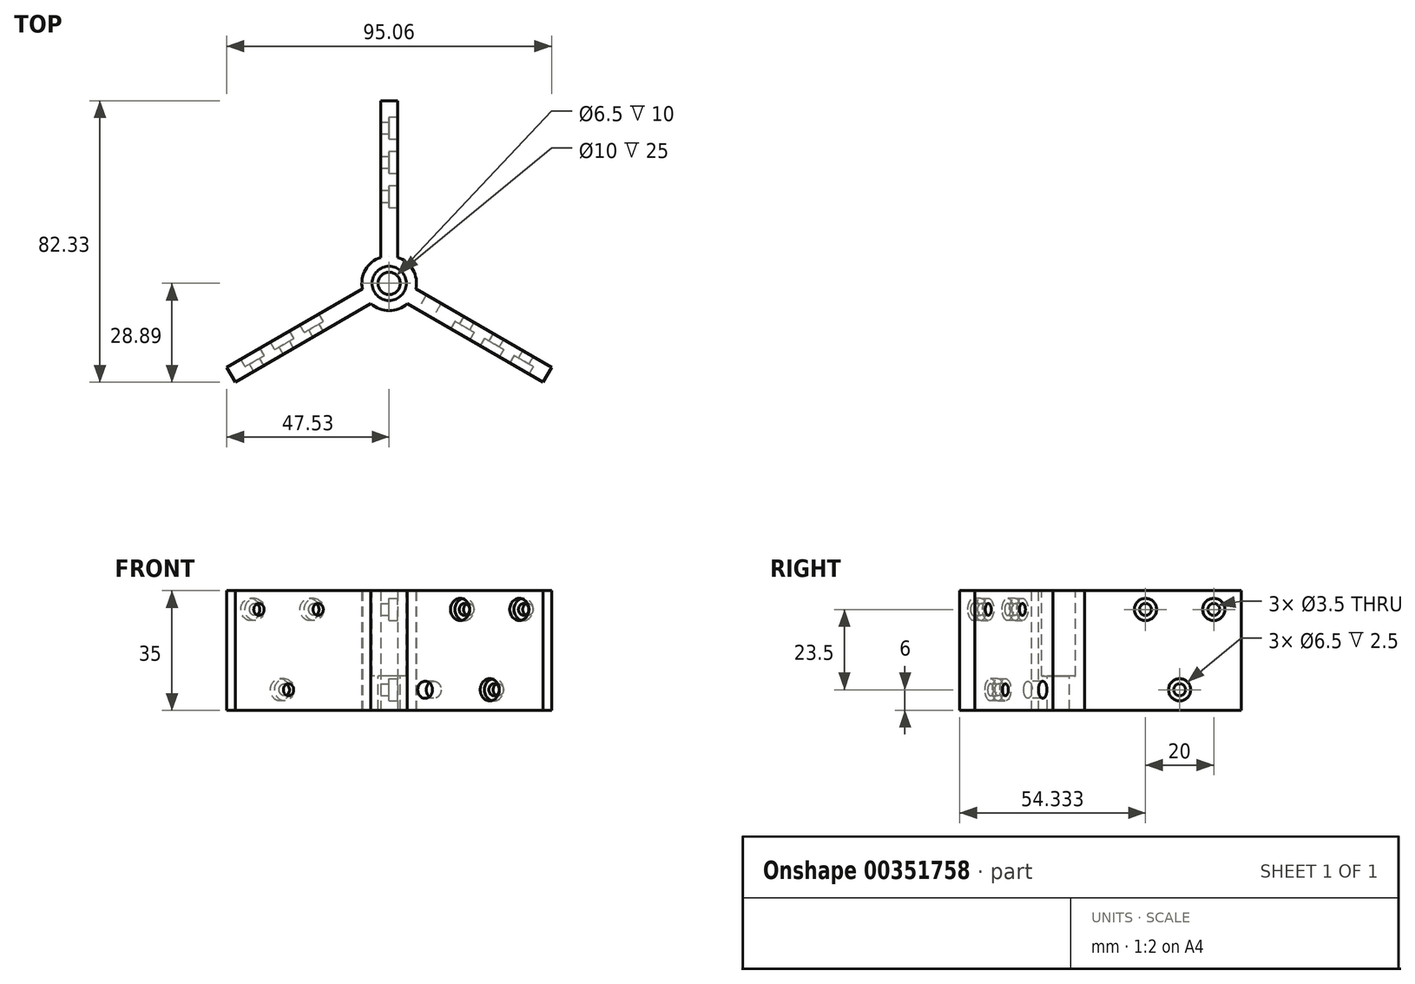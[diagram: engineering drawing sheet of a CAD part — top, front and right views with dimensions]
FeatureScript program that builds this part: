
annotation { "Feature Type Name" : "Feature", "Feature Type Description" : "" }
export const myFeature = defineFeature(function(context is Context, id is Id, definition is map)
    precondition{}
    {
        {
            var Q0;
            Q0=qCreatedBy(makeId("Top.planeOp"),FACE);
            var sketch = newSketch(context, id + "F0", { "sketchPlane" : qUnion([Q0])});
            skCircle(sketch, "E0.cCircle", {"center": v(0, 0) * mm, "radius": 1.44 * mm, "construction": true});
            skLineSegment(sketch, "E0.0", {"start": v(-2.5, 1.44) * mm, "end": v(2.5, 1.44) * mm});
            skLineSegment(sketch, "E0.1", {"start": v(2.5, 1.44) * mm, "end": v(0, -2.89) * mm});
            skLineSegment(sketch, "E0.2", {"start": v(0, -2.89) * mm, "end": v(-2.5, 1.44) * mm});
            skPoint(sketch, "E0.0.midPoint", {"position": v(0, 1.44) * mm});
            skLineSegment(sketch, "E1.top", {"start": v(-2.5, 53.44) * mm, "end": v(2.5, 53.44) * mm});
            skLineSegment(sketch, "E1.left", {"start": v(-2.5, 1.44) * mm, "end": v(-2.5, 53.44) * mm});
            skLineSegment(sketch, "E1.right", {"start": v(2.5, 1.44) * mm, "end": v(2.5, 53.44) * mm});
            skLineSegment(sketch, "E2.1.0", {"start": v(-2.5, 1.44) * mm, "end": v(-47.53, -24.56) * mm});
            skLineSegment(sketch, "E2.1.1", {"start": v(0, -2.89) * mm, "end": v(-45.03, -28.89) * mm});
            skLineSegment(sketch, "E2.1.2", {"start": v(-45.03, -28.89) * mm, "end": v(-47.53, -24.56) * mm});
            skLineSegment(sketch, "E2.2.0", {"start": v(0, -2.89) * mm, "end": v(45.03, -28.89) * mm});
            skLineSegment(sketch, "E2.2.1", {"start": v(2.5, 1.44) * mm, "end": v(47.53, -24.56) * mm});
            skLineSegment(sketch, "E2.2.2", {"start": v(47.53, -24.56) * mm, "end": v(45.03, -28.89) * mm});
            skCircle(sketch, "E3", {"center": v(0, 0) * mm, "radius": 8 * mm});
            skSolve(sketch);
        }
        {
            var Q0;
            {var subQ0=sQuery(id+"F0.wireOp",EDGE,"E0.0");Q0=makeQuery(id+"F0.imprint","IMPRINT",FACE,{"disambiguationData":[TD([[makeQuery(id+"F0.imprint","IMPRINT",EDGE,{"derivedFrom":subQ0}),1.0]])]});}
            var Q1;
            {var subQ0=sQuery(id+"F0.wireOp",EDGE,"E1.top");Q1=makeQuery(id+"F0.imprint","IMPRINT",FACE,{"disambiguationData":[TD([[makeQuery(id+"F0.imprint","IMPRINT",EDGE,{"derivedFrom":subQ0}),-1.0]])]});}
            var Q2;
            {var subQ0=sQuery(id+"F0.wireOp",EDGE,"E0.1");Q2=makeQuery(id+"F0.imprint","IMPRINT",FACE,{"disambiguationData":[TD([[makeQuery(id+"F0.imprint","IMPRINT",EDGE,{"derivedFrom":subQ0}),1.0]])]});}
            var Q3;
            Q3=makeQuery(id+"F0.imprint","IMPRINT",FACE,{"disambiguationData":[TD([[makeQuery(id+"F0.imprint","IMPRINT",EDGE,{"derivedFrom":sQuery(id+"F0.wireOp",EDGE,"E0.0")}),-1.0]])]});
            var Q4;
            {var subQ0=sQuery(id+"F0.wireOp",EDGE,"E0.2");Q4=makeQuery(id+"F0.imprint","IMPRINT",FACE,{"disambiguationData":[TD([[makeQuery(id+"F0.imprint","IMPRINT",EDGE,{"derivedFrom":subQ0}),1.0]])]});}
            var Q5;
            {var subQ3=sQuery(id+"F0.wireOp",EDGE,"E2.2.2");Q5=makeQuery(id+"F0.imprint","IMPRINT",FACE,{"disambiguationData":[TD([[makeQuery(id+"F0.imprint","IMPRINT",EDGE,{"derivedFrom":subQ3}),-1.0]])]});}
            var Q6;
            {var subQ3=sQuery(id+"F0.wireOp",EDGE,"E2.1.2");Q6=makeQuery(id+"F0.imprint","IMPRINT",FACE,{"disambiguationData":[TD([[makeQuery(id+"F0.imprint","IMPRINT",EDGE,{"derivedFrom":subQ3}),-1.0]])]});}
            extrude(context, id + "F1", {"entities" : qUnion([Q0, Q1, Q2, Q3, Q4, Q5, Q6]), "depth" : 35 * mm, "offsetDistance" : 25 * mm});
        }
        {
            var Q0;
            {var subQ1=sQuery(id+"F0.wireOp",EDGE,"E1.left");var subQ3=sQuery(id+"F0.wireOp",EDGE,"E3");var subQ4=makeQuery(id+"F0.imprint","INTERSECT",VERTEX,{"derivedFrom":[subQ1,subQ3]});Q0=makeQuery(id+"F0.imprint","IMPRINT",FACE,{"disambiguationData":[TD([[makeQuery(id+"F0.imprint","IMPRINT",EDGE,{"disambiguationData":[TD([[subQ4,-1.0]])],"derivedFrom":subQ3}),1.0]])]});}
            var Q1;
            {var subQ1=sQuery(id+"F0.wireOp",EDGE,"E1.right");var subQ3=sQuery(id+"F0.wireOp",EDGE,"E3");var subQ4=makeQuery(id+"F0.imprint","INTERSECT",VERTEX,{"derivedFrom":[subQ1,subQ3]});Q1=makeQuery(id+"F0.imprint","IMPRINT",FACE,{"disambiguationData":[TD([[makeQuery(id+"F0.imprint","IMPRINT",EDGE,{"disambiguationData":[TD([[subQ4,1.0]])],"derivedFrom":subQ3}),1.0]])]});}
            var Q2;
            {var subQ1=sQuery(id+"F0.wireOp",EDGE,"E2.1.1");var subQ3=sQuery(id+"F0.wireOp",EDGE,"E3");var subQ4=makeQuery(id+"F0.imprint","INTERSECT",VERTEX,{"derivedFrom":[subQ1,subQ3]});Q2=makeQuery(id+"F0.imprint","IMPRINT",FACE,{"disambiguationData":[TD([[makeQuery(id+"F0.imprint","IMPRINT",EDGE,{"disambiguationData":[TD([[subQ4,-1.0]])],"derivedFrom":subQ3}),1.0]])]});}
            extrude(context, id + "F2", {"entities" : qUnion([Q0, Q1, Q2]), "operationType" : NewBodyOperationType.ADD, "depth" : 35 * mm, "offsetDistance" : 25 * mm});
        }
        {
            var Q0;
            Q0=makeQuery(id+"F1.opExtrude","SWEPT_FACE",FACE,{"disambiguationData":[OSD([sQuery(id+"F0.wireOp",EDGE,"E2.2.0")])]});
            var sketch = newSketch(context, id + "F3", { "sketchPlane" : qUnion([Q0])});
            skCircle(sketch, "E4", {"center": v(25.44, 29.5) * mm, "radius": 8.18 * mm});
            skCircle(sketch, "E5", {"center": v(45.44, 29.5) * mm, "radius": 8.88 * mm});
            skCircle(sketch, "E6", {"center": v(35.44, 6) * mm, "radius": 8.24 * mm});
            skCircle(sketch, "E7", {"center": v(13.6, 6) * mm, "radius": 2.5 * mm});
            skSolve(sketch);
        }
        {
            var Q0;
            Q0=makeQuery(id+"F1.opExtrude","SWEPT_FACE",FACE,{"disambiguationData":[OSD([sQuery(id+"F0.wireOp",EDGE,"E1.right")])]});
            var sketch = newSketch(context, id + "F4", { "sketchPlane" : qUnion([Q0])});
            skCircle(sketch, "E8", {"center": v(25.44, 29.5) * mm, "radius": 3.54 * mm});
            skCircle(sketch, "E9", {"center": v(45.44, 29.5) * mm, "radius": 6.4 * mm});
            skCircle(sketch, "E10", {"center": v(35.44, 6) * mm, "radius": 7.3 * mm});
            skSolve(sketch);
        }
        {
            var Q0;
            Q0=makeQuery(id+"F1.opExtrude","SWEPT_FACE",FACE,{"disambiguationData":[OSD([sQuery(id+"F0.wireOp",EDGE,"E2.1.0")])]});
            var sketch = newSketch(context, id + "F5", { "sketchPlane" : qUnion([Q0])});
            skCircle(sketch, "E11", {"center": v(25.44, 29.5) * mm, "radius": 4.06 * mm});
            skCircle(sketch, "E12", {"center": v(45.44, 29.5) * mm, "radius": 3.4 * mm});
            skCircle(sketch, "E13", {"center": v(35.44, 6) * mm, "radius": 3.73 * mm});
            skSolve(sketch);
        }
        {
            var Q0;
            Q0=sQuery(id+"F3.wireOp",VERTEX,"E4.center");
            var Q1;
            Q1=sQuery(id+"F3.wireOp",VERTEX,"E5.center");
            var Q2;
            Q2=sQuery(id+"F3.wireOp",VERTEX,"E6.center");
            var Q3;
            Q3=makeQuery(id+"F1.opExtrude","SWEPT_BODY",BODY,{"disambiguationData":[OSD([sQuery(id+"F0.wireOp",EDGE,"E1.top"),sQuery(id+"F0.wireOp",EDGE,"E1.left"),sQuery(id+"F0.wireOp",EDGE,"E1.right"),sQuery(id+"F0.wireOp",EDGE,"E2.1.0"),sQuery(id+"F0.wireOp",EDGE,"E2.1.1"),sQuery(id+"F0.wireOp",EDGE,"E2.1.2"),sQuery(id+"F0.wireOp",EDGE,"E2.2.0"),sQuery(id+"F0.wireOp",EDGE,"E2.2.1"),sQuery(id+"F0.wireOp",EDGE,"E2.2.2")])]});
            hole(context, id + "F6", {"style" : HoleStyle.C_BORE, "endStyle" : HoleEndStyle.BLIND, "holeDiameter" : 3.5 * mm, "cBoreDiameter" : 6.5 * mm, "cBoreDepth" : 2.5 * mm, "majorDiameter" : 5 * mm, "holeDepth" : 12 * mm, "isTappedThrough" : true, "tappedDepth" : 12 * mm, "tapClearance" : 3, "locations" : qUnion([Q0, Q1, Q2]), "scope" : qUnion([Q3])});
        }
        {
            var Q0;
            Q0=sQuery(id+"F4.wireOp",VERTEX,"E8.center");
            var Q1;
            Q1=sQuery(id+"F4.wireOp",VERTEX,"E9.center");
            var Q2;
            Q2=sQuery(id+"F4.wireOp",VERTEX,"E10.center");
            var Q3;
            Q3=makeQuery(id+"F1.opExtrude","SWEPT_BODY",BODY,{"disambiguationData":[OSD([sQuery(id+"F0.wireOp",EDGE,"E1.top"),sQuery(id+"F0.wireOp",EDGE,"E1.left"),sQuery(id+"F0.wireOp",EDGE,"E1.right"),sQuery(id+"F0.wireOp",EDGE,"E2.1.0"),sQuery(id+"F0.wireOp",EDGE,"E2.1.1"),sQuery(id+"F0.wireOp",EDGE,"E2.1.2"),sQuery(id+"F0.wireOp",EDGE,"E2.2.0"),sQuery(id+"F0.wireOp",EDGE,"E2.2.1"),sQuery(id+"F0.wireOp",EDGE,"E2.2.2")])]});
            hole(context, id + "F7", {"style" : HoleStyle.C_BORE, "endStyle" : HoleEndStyle.BLIND, "holeDiameter" : 3.5 * mm, "cBoreDiameter" : 6.5 * mm, "cBoreDepth" : 2.5 * mm, "majorDiameter" : 5 * mm, "holeDepth" : 12 * mm, "isTappedThrough" : true, "tappedDepth" : 12 * mm, "tapClearance" : 3, "locations" : qUnion([Q0, Q1, Q2]), "scope" : qUnion([Q3])});
        }
        {
            var Q0;
            Q0=sQuery(id+"F5.wireOp",VERTEX,"E11.center");
            var Q1;
            Q1=sQuery(id+"F5.wireOp",VERTEX,"E12.center");
            var Q2;
            Q2=sQuery(id+"F5.wireOp",VERTEX,"E13.center");
            var Q3;
            Q3=makeQuery(id+"F1.opExtrude","SWEPT_BODY",BODY,{"disambiguationData":[OSD([sQuery(id+"F0.wireOp",EDGE,"E1.top"),sQuery(id+"F0.wireOp",EDGE,"E1.left"),sQuery(id+"F0.wireOp",EDGE,"E1.right"),sQuery(id+"F0.wireOp",EDGE,"E2.1.0"),sQuery(id+"F0.wireOp",EDGE,"E2.1.1"),sQuery(id+"F0.wireOp",EDGE,"E2.1.2"),sQuery(id+"F0.wireOp",EDGE,"E2.2.0"),sQuery(id+"F0.wireOp",EDGE,"E2.2.1"),sQuery(id+"F0.wireOp",EDGE,"E2.2.2")])]});
            hole(context, id + "F8", {"style" : HoleStyle.C_BORE, "endStyle" : HoleEndStyle.BLIND, "holeDiameter" : 3.5 * mm, "cBoreDiameter" : 6.5 * mm, "cBoreDepth" : 2.5 * mm, "majorDiameter" : 5 * mm, "holeDepth" : 12 * mm, "isTappedThrough" : true, "tappedDepth" : 12 * mm, "tapClearance" : 3, "locations" : qUnion([Q0, Q1, Q2]), "scope" : qUnion([Q3])});
        }
        {
            var Q0;
            Q0=makeQuery(id+"F3.imprint","IMPRINT",FACE,{"disambiguationData":[TD([[makeQuery(id+"F3.imprint","IMPRINT",EDGE,{"derivedFrom":sQuery(id+"F3.wireOp",EDGE,"E7")}),1.0]])]});
            extrude(context, id + "F9", {"entities" : qUnion([Q0]), "operationType" : NewBodyOperationType.REMOVE, "oppositeDirection" : true, "depth" : 25 * mm, "offsetDistance" : 25 * mm});
        }
        {
            var Q0;
            {var subQ0=sQuery(id+"F0.wireOp",EDGE,"E3");var subQ1=sQuery(id+"F0.wireOp",EDGE,"E2.2.0");var subQ2=sQuery(id+"F0.wireOp",EDGE,"E2.1.1");var subQ3=sQuery(id+"F0.wireOp",EDGE,"E2.2.1");var subQ4=sQuery(id+"F0.wireOp",EDGE,"E1.right");var subQ5=sQuery(id+"F0.wireOp",EDGE,"E2.1.0");var subQ6=sQuery(id+"F0.wireOp",EDGE,"E1.left");Q0=makeQuery(id+"F2.boolean.opBoolean","MERGE",FACE,{"derivedFrom":[makeQuery(id+"F1.opExtrude","CAP_FACE",FACE,{"disambiguationData":[OSD([sQuery(id+"F0.wireOp",EDGE,"E1.top"),subQ6,subQ4,subQ5,subQ2,sQuery(id+"F0.wireOp",EDGE,"E2.1.2"),subQ1,subQ3,sQuery(id+"F0.wireOp",EDGE,"E2.2.2")])],"isStart":false}),makeQuery(id+"F2.opExtrude","CAP_FACE",FACE,{"disambiguationData":[OSD([subQ6,subQ5,subQ0])],"isStart":false}),makeQuery(id+"F2.opExtrude","CAP_FACE",FACE,{"disambiguationData":[OSD([subQ4,subQ3,subQ0])],"isStart":false}),makeQuery(id+"F2.opExtrude","CAP_FACE",FACE,{"disambiguationData":[OSD([subQ2,subQ1,subQ0])],"isStart":false})]});}
            var sketch = newSketch(context, id + "F10", { "sketchPlane" : qUnion([Q0])});
            skCircle(sketch, "E14", {"center": v(0, 0) * mm, "radius": 6.4 * mm});
            skSolve(sketch);
        }
        {
            var Q0;
            Q0=sQuery(id+"F10.wireOp",VERTEX,"E14.center");
            var Q1;
            Q1=makeQuery(id+"F1.opExtrude","SWEPT_BODY",BODY,{"disambiguationData":[OSD([sQuery(id+"F0.wireOp",EDGE,"E1.top"),sQuery(id+"F0.wireOp",EDGE,"E1.left"),sQuery(id+"F0.wireOp",EDGE,"E1.right"),sQuery(id+"F0.wireOp",EDGE,"E2.1.0"),sQuery(id+"F0.wireOp",EDGE,"E2.1.1"),sQuery(id+"F0.wireOp",EDGE,"E2.1.2"),sQuery(id+"F0.wireOp",EDGE,"E2.2.0"),sQuery(id+"F0.wireOp",EDGE,"E2.2.1"),sQuery(id+"F0.wireOp",EDGE,"E2.2.2")])]});
            hole(context, id + "F11", {"style" : HoleStyle.C_BORE, "endStyle" : HoleEndStyle.BLIND, "holeDiameter" : 6.5 * mm, "cBoreDiameter" : 10 * mm, "cBoreDepth" : 25 * mm, "majorDiameter" : 5 * mm, "holeDepth" : 35 * mm, "isTappedThrough" : true, "tappedDepth" : 12 * mm, "tapClearance" : 3, "locations" : qUnion([Q0]), "scope" : qUnion([Q1])});
        }
    });
